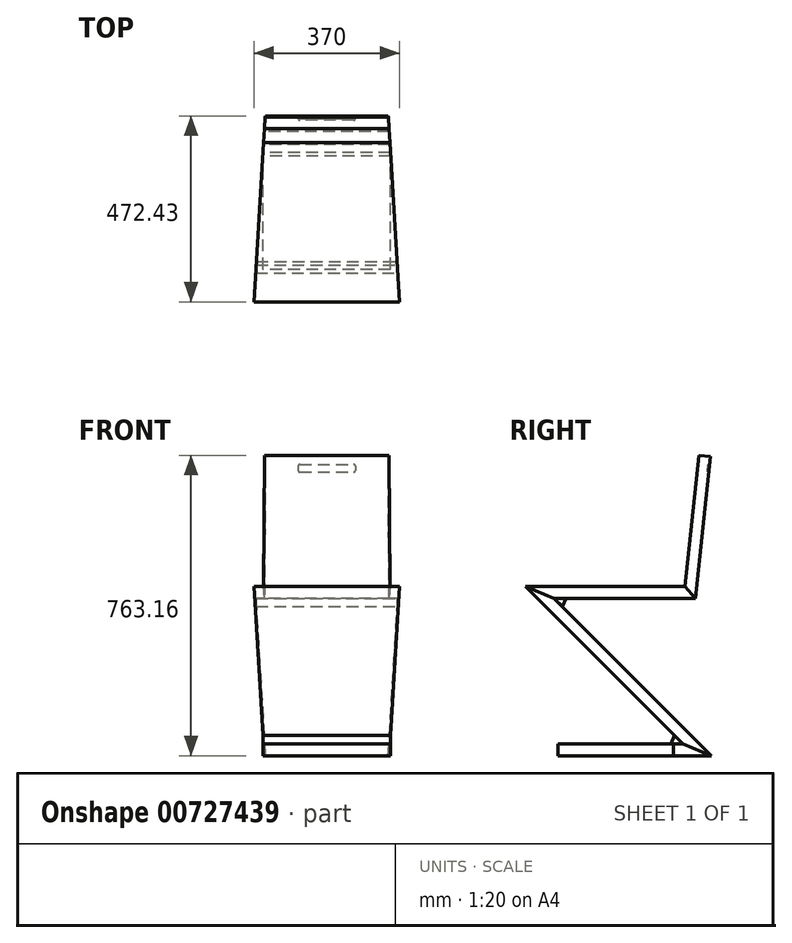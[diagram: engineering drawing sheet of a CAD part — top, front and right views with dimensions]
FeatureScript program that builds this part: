
annotation { "Feature Type Name" : "Feature", "Feature Type Description" : "" }
export const myFeature = defineFeature(function(context is Context, id is Id, definition is map)
    precondition{}
    {
        {
            var Q0;
            Q0=qCreatedBy(makeId("Right.planeOp"),FACE);
            var sketch = newSketch(context, id + "F0", { "sketchPlane" : qUnion([Q0])});
            skLineSegment(sketch, "E0", {"start": v(0, 0) * mm, "end": v(390, 0) * mm});
            skLineSegment(sketch, "E1", {"start": v(390, 0) * mm, "end": v(-10, 400) * mm});
            skLineSegment(sketch, "E2", {"start": v(-10, 400) * mm, "end": v(349.59, 400) * mm});
            skLineSegment(sketch, "E3", {"start": v(349.59, 400) * mm, "end": v(387.43, 760.03) * mm});
            skLineSegment(sketch, "E4", {"start": v(0, 30) * mm, "end": v(317.57, 30) * mm});
            skLineSegment(sketch, "E5", {"start": v(317.57, 30) * mm, "end": v(-82.43, 430) * mm});
            skLineSegment(sketch, "E6", {"start": v(-82.43, 430) * mm, "end": v(322.57, 430) * mm});
            skLineSegment(sketch, "E7", {"start": v(322.57, 430) * mm, "end": v(357.6, 763.16) * mm});
            skLineSegment(sketch, "E8", {"start": v(0, 30) * mm, "end": v(0, 0) * mm});
            skLineSegment(sketch, "E9", {"start": v(357.6, 763.16) * mm, "end": v(387.43, 760.03) * mm});
            skLineSegment(sketch, "E10", {"start": v(-82.43, 430) * mm, "end": v(-10, 400) * mm});
            skLineSegment(sketch, "E11", {"start": v(322.57, 430) * mm, "end": v(349.59, 400) * mm});
            skLineSegment(sketch, "E12", {"start": v(317.57, 30) * mm, "end": v(390, 0) * mm});
            skCircle(sketch, "E13", {"center": v(-10, 400) * mm, "radius": 30 * mm, "construction": true});
            skLineSegment(sketch, "E14", {"start": v(11.21, 378.79) * mm, "end": v(20, 400) * mm});
            skCircle(sketch, "E15", {"center": v(317.57, 30) * mm, "radius": 30 * mm, "construction": true});
            skLineSegment(sketch, "E16", {"start": v(287.57, 30) * mm, "end": v(296.36, 51.21) * mm});
            skSolve(sketch);
        }
        {
            var Q0;
            Q0=makeQuery(id+"F0.imprint","IMPRINT",FACE,{"disambiguationData":[TD([[makeQuery(id+"F0.imprint","IMPRINT",EDGE,{"derivedFrom":sQuery(id+"F0.wireOp",EDGE,"E3")}),1.0]])]});
            extrude(context, id + "F1", {"entities" : qUnion([Q0]), "endBound" : BoundingType.SYMMETRIC, "depth" : 324 * mm, "offsetDistance" : 25 * mm});
        }
        {
            var Q0;
            Q0=makeQuery(id+"F0.imprint","IMPRINT",FACE,{"disambiguationData":[TD([[makeQuery(id+"F0.imprint","IMPRINT",EDGE,{"derivedFrom":sQuery(id+"F0.wireOp",EDGE,"E0")}),1.0]])]});
            extrude(context, id + "F2", {"entities" : qUnion([Q0]), "endBound" : BoundingType.SYMMETRIC, "depth" : 324 * mm, "offsetDistance" : 25 * mm});
        }
        {
            var Q0;
            Q0=makeQuery(id+"F0.imprint","IMPRINT",FACE,{"disambiguationData":[TD([[makeQuery(id+"F0.imprint","IMPRINT",EDGE,{"derivedFrom":sQuery(id+"F0.wireOp",EDGE,"E6")}),-1.0]])]});
            extrude(context, id + "F3", {"entities" : qUnion([Q0]), "endBound" : BoundingType.SYMMETRIC, "depth" : 370 * mm, "offsetDistance" : 25 * mm});
        }
        {
            var Q0;
            {var subQ0=sQuery(id+"F0.wireOp",EDGE,"E10");Q0=makeQuery(id+"F0.imprint","IMPRINT",FACE,{"disambiguationData":[TD([[makeQuery(id+"F0.imprint","IMPRINT",EDGE,{"derivedFrom":subQ0}),-1.0]])]});}
            extrude(context, id + "F4", {"entities" : qUnion([Q0]), "endBound" : BoundingType.SYMMETRIC, "depth" : 370 * mm, "offsetDistance" : 25 * mm});
        }
        {
            var Q0;
            {var subQ3=sQuery(id+"F0.wireOp",EDGE,"E16");Q0=makeQuery(id+"F0.imprint","IMPRINT",FACE,{"disambiguationData":[TD([[makeQuery(id+"F0.imprint","IMPRINT",EDGE,{"derivedFrom":subQ3}),-1.0]])]});}
            var Q1;
            Q1=makeQuery(id+"F4.opExtrude","CAP_FACE",FACE,{"disambiguationData":[OSD([sQuery(id+"F0.wireOp",EDGE,"E1"),sQuery(id+"F0.wireOp",EDGE,"E5"),sQuery(id+"F0.wireOp",EDGE,"E10"),sQuery(id+"F0.wireOp",EDGE,"E12")])],"isStart":false});
            var Q2;
            Q2=makeQuery(id+"F4.opExtrude","CAP_FACE",FACE,{"disambiguationData":[OSD([sQuery(id+"F0.wireOp",EDGE,"E1"),sQuery(id+"F0.wireOp",EDGE,"E5"),sQuery(id+"F0.wireOp",EDGE,"E10"),sQuery(id+"F0.wireOp",EDGE,"E12")])],"isStart":true});
            extrude(context, id + "F5", {"entities" : qUnion([Q0]), "endBound" : BoundingType.UP_TO_SURFACE, "depth" : 25 * mm, "endBoundEntityFace" : qUnion([Q1]), "offsetDistance" : 25 * mm, "hasSecondDirection" : true, "secondDirectionBound" : SecondDirectionBoundingType.UP_TO_SURFACE, "secondDirectionOppositeDirection" : true, "secondDirectionDepth" : 25 * mm, "secondDirectionBoundEntityFace" : qUnion([Q2])});
        }
        {
            var Q0;
            {var subQ3=sQuery(id+"F0.wireOp",EDGE,"E14");Q0=makeQuery(id+"F0.imprint","IMPRINT",FACE,{"disambiguationData":[TD([[makeQuery(id+"F0.imprint","IMPRINT",EDGE,{"derivedFrom":subQ3}),1.0]])]});}
            var Q1;
            Q1=makeQuery(id+"F3.opExtrude","CAP_FACE",FACE,{"disambiguationData":[OSD([sQuery(id+"F0.wireOp",EDGE,"E2"),sQuery(id+"F0.wireOp",EDGE,"E6"),sQuery(id+"F0.wireOp",EDGE,"E10"),sQuery(id+"F0.wireOp",EDGE,"E11")])],"isStart":true});
            var Q2;
            Q2=makeQuery(id+"F3.opExtrude","CAP_FACE",FACE,{"disambiguationData":[OSD([sQuery(id+"F0.wireOp",EDGE,"E2"),sQuery(id+"F0.wireOp",EDGE,"E6"),sQuery(id+"F0.wireOp",EDGE,"E10"),sQuery(id+"F0.wireOp",EDGE,"E11")])],"isStart":false});
            extrude(context, id + "F6", {"entities" : qUnion([Q0]), "endBound" : BoundingType.UP_TO_SURFACE, "oppositeDirection" : true, "depth" : 25 * mm, "endBoundEntityFace" : qUnion([Q1]), "offsetDistance" : 25 * mm, "hasSecondDirection" : true, "secondDirectionBound" : SecondDirectionBoundingType.UP_TO_SURFACE, "secondDirectionOppositeDirection" : false, "secondDirectionDepth" : 25 * mm, "secondDirectionBoundEntityFace" : qUnion([Q2])});
        }
        {
            var Q0;
            Q0=qCreatedBy(makeId("Top.planeOp"),FACE);
            var sketch = newSketch(context, id + "F7", { "sketchPlane" : qUnion([Q0])});
            skLineSegment(sketch, "E17", {"start": v(-185, -82.43) * mm, "end": v(-149.7, 494.67) * mm});
            skLineSegment(sketch, "E18", {"start": v(-149.7, 494.67) * mm, "end": v(-227.65, 499.44) * mm});
            skLineSegment(sketch, "E19", {"start": v(-227.65, 499.44) * mm, "end": v(-310.79, -330.91) * mm});
            skLineSegment(sketch, "E20", {"start": v(-310.79, -330.91) * mm, "end": v(-185, -82.43) * mm});
            skSolve(sketch);
        }
        {
            var Q0;
            Q0 = qSketchRegion(id + "F7", true);
            extrude(context, id + "F8", {"entities" : qUnion([Q0]), "depth" : 1053 * mm, "offsetDistance" : 25 * mm});
        }
        {
            var Q0;
            Q0=makeQuery(id+"F8.opExtrude","SWEPT_BODY",BODY,{"disambiguationData":[OSD([sQuery(id+"F7.wireOp",EDGE,"E17"),sQuery(id+"F7.wireOp",EDGE,"E18"),sQuery(id+"F7.wireOp",EDGE,"E19"),sQuery(id+"F7.wireOp",EDGE,"E20")])]});
            var Q1;
            Q1=qCreatedBy(makeId("Right.planeOp"),FACE);
            mirror(context, id + "F9", {"entities" : qUnion([Q0]), "mirrorPlane" : qUnion([Q1])});
        }
        {
            var Q0;
            Q0=makeQuery(id+"F8.opExtrude","SWEPT_BODY",BODY,{"disambiguationData":[OSD([sQuery(id+"F7.wireOp",EDGE,"E17"),sQuery(id+"F7.wireOp",EDGE,"E18"),sQuery(id+"F7.wireOp",EDGE,"E19"),sQuery(id+"F7.wireOp",EDGE,"E20")])]});
            var Q1;
            Q1=makeQuery(id+"F9.opPattern","COPY",BODY,{"derivedFrom":makeQuery(id+"F8.opExtrude","SWEPT_BODY",BODY,{"disambiguationData":[OSD([sQuery(id+"F7.wireOp",EDGE,"E17"),sQuery(id+"F7.wireOp",EDGE,"E18"),sQuery(id+"F7.wireOp",EDGE,"E19"),sQuery(id+"F7.wireOp",EDGE,"E20")])]}),"instanceName":"1"});
            var Q2;
            Q2=makeQuery(id+"F2.opExtrude","SWEPT_BODY",BODY,{"disambiguationData":[OSD([sQuery(id+"F0.wireOp",EDGE,"E0"),sQuery(id+"F0.wireOp",EDGE,"E4"),sQuery(id+"F0.wireOp",EDGE,"E8"),sQuery(id+"F0.wireOp",EDGE,"E12")])]});
            var Q3;
            Q3=makeQuery(id+"F3.opExtrude","SWEPT_BODY",BODY,{"disambiguationData":[OSD([sQuery(id+"F0.wireOp",EDGE,"E2"),sQuery(id+"F0.wireOp",EDGE,"E6"),sQuery(id+"F0.wireOp",EDGE,"E10"),sQuery(id+"F0.wireOp",EDGE,"E11")])]});
            var Q4;
            Q4=makeQuery(id+"F1.opExtrude","SWEPT_BODY",BODY,{"disambiguationData":[OSD([sQuery(id+"F0.wireOp",EDGE,"E3"),sQuery(id+"F0.wireOp",EDGE,"E7"),sQuery(id+"F0.wireOp",EDGE,"E9"),sQuery(id+"F0.wireOp",EDGE,"E11")])]});
            var Q5;
            Q5=makeQuery(id+"F4.opExtrude","SWEPT_BODY",BODY,{"disambiguationData":[OSD([sQuery(id+"F0.wireOp",EDGE,"E1"),sQuery(id+"F0.wireOp",EDGE,"E5"),sQuery(id+"F0.wireOp",EDGE,"E10"),sQuery(id+"F0.wireOp",EDGE,"E12")])]});
            var Q6;
            Q6=makeQuery(id+"F5.opExtrude","SWEPT_BODY",BODY,{"disambiguationData":[OSD([sQuery(id+"F0.wireOp",EDGE,"E4"),sQuery(id+"F0.wireOp",EDGE,"E5"),sQuery(id+"F0.wireOp",EDGE,"E16")])]});
            var Q7;
            Q7=makeQuery(id+"F6.opExtrude","SWEPT_BODY",BODY,{"disambiguationData":[OSD([sQuery(id+"F0.wireOp",EDGE,"E1"),sQuery(id+"F0.wireOp",EDGE,"E2"),sQuery(id+"F0.wireOp",EDGE,"E14")])]});
            booleanBodies(context, id + "F10", {"operationType" : BooleanOperationType.SUBTRACTION, "tools" : qUnion([Q0, Q1]), "targets" : qUnion([Q2, Q3, Q4, Q5, Q6, Q7])});
        }
        {
            var Q0;
            Q0=makeQuery(id+"F1.opExtrude","SWEPT_FACE",FACE,{"disambiguationData":[OSD([sQuery(id+"F0.wireOp",EDGE,"E3")])]});
            var sketch = newSketch(context, id + "F11", { "sketchPlane" : qUnion([Q0])});
            skLineSegment(sketch, "E21.bottom", {"start": v(72.5, 776.36) * mm, "end": v(-72.5, 776.36) * mm});
            skLineSegment(sketch, "E21.top", {"start": v(72.5, 756.36) * mm, "end": v(-72.5, 756.36) * mm});
            skLineSegment(sketch, "E21.left", {"start": v(72.5, 776.36) * mm, "end": v(72.5, 756.36) * mm});
            skLineSegment(sketch, "E21.right", {"start": v(-72.5, 776.36) * mm, "end": v(-72.5, 756.36) * mm});
            skLineSegment(sketch, "E22", {"start": v(0, 796.36) * mm, "end": v(0, 776.36) * mm, "construction": true});
            skSolve(sketch);
        }
        {
            var Q0;
            Q0 = qSketchRegion(id + "F11", true);
            extrude(context, id + "F12", {"entities" : qUnion([Q0]), "operationType" : NewBodyOperationType.REMOVE, "oppositeDirection" : true, "depth" : 5 * mm, "offsetDistance" : 25 * mm});
        }
        {
            var Q0;
            Q0=makeQuery(id+"F12.boolean.opBoolean","COPY",FACE,{"derivedFrom":makeQuery(id+"F12.opExtrude","CAP_FACE",FACE,{"disambiguationData":[OSD([sQuery(id+"F11.wireOp",EDGE,"E21.bottom"),sQuery(id+"F11.wireOp",EDGE,"E21.top"),sQuery(id+"F11.wireOp",EDGE,"E21.left"),sQuery(id+"F11.wireOp",EDGE,"E21.right")])],"isStart":false})});
            var Q1;
            Q1=makeQuery(id+"F12.boolean.opBoolean","COPY",EDGE,{"derivedFrom":makeQuery(id+"F12.opExtrude","SWEPT_EDGE",EDGE,{"disambiguationData":[OSD([sQuery(id+"F11.wireOp",EDGE,"E21.bottom"),sQuery(id+"F11.wireOp",EDGE,"E21.left")])]})});
            var Q2;
            Q2=makeQuery(id+"F12.boolean.opBoolean","COPY",EDGE,{"derivedFrom":makeQuery(id+"F12.opExtrude","SWEPT_EDGE",EDGE,{"disambiguationData":[OSD([sQuery(id+"F11.wireOp",EDGE,"E21.top"),sQuery(id+"F11.wireOp",EDGE,"E21.left")])]})});
            var Q3;
            Q3=makeQuery(id+"F12.boolean.opBoolean","COPY",EDGE,{"derivedFrom":makeQuery(id+"F12.opExtrude","SWEPT_EDGE",EDGE,{"disambiguationData":[OSD([sQuery(id+"F11.wireOp",EDGE,"E21.bottom"),sQuery(id+"F11.wireOp",EDGE,"E21.right")])]})});
            var Q4;
            Q4=makeQuery(id+"F12.boolean.opBoolean","COPY",EDGE,{"derivedFrom":makeQuery(id+"F12.opExtrude","SWEPT_EDGE",EDGE,{"disambiguationData":[OSD([sQuery(id+"F11.wireOp",EDGE,"E21.top"),sQuery(id+"F11.wireOp",EDGE,"E21.right")])]})});
            fillet(context, id + "F13", {"entities" : qUnion([Q0, Q1, Q2, Q3, Q4]), "radius" : 4 * mm, "tangentPropagation" : true, "allowEdgeOverflow" : false});
        }
    });
